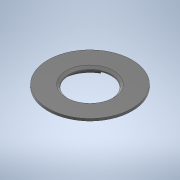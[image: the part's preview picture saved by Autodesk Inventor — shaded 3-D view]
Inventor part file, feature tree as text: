
AUTODESK INVENTOR PART (.ipt)
format: ipt  version: 2020 (Build 240168000, 168)  size: 232,448 bytes
history: native  units: mm
features: sketch x4, projected_geometry x4, revolve x2, chamfer x2, extrude x2, other x1, pattern_circular x1
ambient origin geometry x8: Origin, YZ Plane, XZ Plane, XY Plane, X Axis, Y Axis, Z Axis, Center Point
bodies: Body1 (feature_tree)
feature tree (16):
  other  "Твердое тело1"
  revolve  "Вращение1"
  chamfer  "Фаска1"  Distance=19.0mm
  chamfer  "Фаска2"  Distance=27.3mm
  revolve  "Вращение2"
  pattern_circular  "Круговой массив1"  [2 undecoded]
  extrude  "Выдавливание1"  TaperAngle=90.0deg  [1 undecoded]
  extrude  "Выдавливание2"  Depth=2.0mm TaperAngle=45.0deg
  sketch  "Эскиз1"
  sketch  "Эскиз2"
  sketch  "Эскиз3"
  projected_geometry  "Спроецированная петля1"
  projected_geometry  "Спроецированная петля2"
  projected_geometry  "Спроецированная петля3"
  sketch  "Эскиз4"
  projected_geometry  "Спроецированная петля4"
note: 3 required parameter values undecoded (feature->parameter linkage not recoverable at this tier; creation-order binding heuristic only, values carry confidence <= 0.55)
